# Revit family: Deca_Ducha higiênica com registro e derivação_Duna Classica_1984.64.ACT.R
name_source: partatom
category: Plumbing Fixtures
units: mm (PartAtom-declared; Revit-internal decimal feet)

## family parameters
Cut with Voids When Loaded = No
Host = Face
Part Type = Normal
Room Calculation Point = No
Round Connector Dimension = Use Radius
Shared = No

## types (3) — shared parameters
Acompanha o Produto = Acompanha Parafuso e bucha para fixação
Aprovado por = quattroD
Atendimento ao Cliente = 0800-0117073
Categoria = METAIS PARA BANHEIRO
Composição Anel Vedação = -
Composição Assento = -
Composição Básica = Liga cobre (bronze e latão),Aço,Plástico de Engenharia,Elastômeros
Composição Componente = -
Consumo = -
Cor Interna = -
Cores Componente = -
Criado por = quattroD
Código Pai = 1984.64.ACT.R
Default Elevation = 0.7 m
Description = Ducha higiênica com registro e derivação
Diâmetro Água Fria = 0.02 m
Informações Complementares = -
Itens de Instalação = -
Linha = Duna Classica
Manufacturer = Deca
Norma = NBR14877
Pressão máx. funcionamento = 40 MCA
Pressão mín. Aquec. Acúmulo = -
Pressão mín. Aquec. Passagem = -
Pressão mín. funcionamento = 2 MCA
Raio Água Fria = 0.01 m
Saída de Esgoto = -
Segmento = Banheiro Luxo
Tipo de dispositivo economizador = Sim
Tipo de mecanismo utilizado = MVC -1/4 volta
Tipo de rosca de entrada = BSP NBR 8133
Tipo de rosca de saída = -
URL = www.deca.com.br
Vazão na Pressão máx. (L/min) = 6
Vazão na Pressão mín. (L/min) = 4

## per-type parameters (varying)
| type | Cor Principal | Cor Secundária | Material | Material Secundário | Model | Peso Líquido (Kg) |
| 1984.BL64.ACT.MT_Black Matte | Black Matte | - | Deca_Black Matte | Deca_Black Matte | 1984.BL64.ACT.MT | 1.232 |
| 1984.CT64.ACT.MT_Corten | Corten | Branco | Deca_Corten | Deca_Plástico - Branco | 1984.CT64.ACT.MT | 1.231 |
| 1984.GL64.ACT.RD_Red Gold | Red Gold | Branco | Deca_Red Gold | Deca_Plástico - Branco | 1984.GL64.ACT.RD | 1.221 |

note: source unit labels omitted for Vazão na Pressão máx. (L/min), Vazão na Pressão mín. (L/min) — the stored unit's dimension contradicts the parameter name (converter mislabeling)

## geometry (parser evidence)
native form markers: Sweep x3
no freeform markers — native parametric forms only
